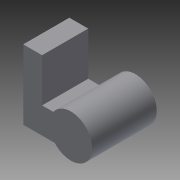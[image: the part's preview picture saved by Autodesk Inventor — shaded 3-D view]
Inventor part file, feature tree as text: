
AUTODESK INVENTOR PART (.ipt)
format: ipt  version: 2015 (Build 190159000, 159)  size: 103,424 bytes
history: native  units: in
note: dims shown in document units (in); Inventor stores cm internally (conversion verified against a paired STEP export)
features: extrude x2, sketch x2, mirror x1, reference x1
ambient origin geometry x8: Origin, YZ Plane, XZ Plane, XY Plane, X Axis, Y Axis, Z Axis, Center Point
bodies: Solid1 (feature_tree)
feature tree (6):
  extrude  "Extrusion1"  Depth=0.9375in TaperAngle=0.0deg
  extrude  "Extrusion2"  [1 undecoded]
  mirror  "Mirror1"
  sketch  "Sketch1"  dims[d0=0.375in d1=0.0in d2=0.9375in d3=0.0in]
  reference  "Reference1"
  sketch  "Sketch2"
note: 1 required parameter value undecoded (feature->parameter linkage not recoverable at this tier; creation-order binding heuristic only, values carry confidence <= 0.55)
